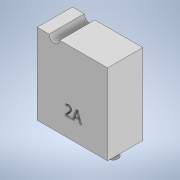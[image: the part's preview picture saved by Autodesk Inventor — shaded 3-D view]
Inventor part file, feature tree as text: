
AUTODESK INVENTOR PART (.ipt)
format: ipt  version: 2021 (Build 250183000, 183)  size: 163,328 bytes
history: native  units: mm
features: sketch x4, extrude x3, emboss x1
ambient origin geometry x8: Origin, YZ Plane, XZ Plane, XY Plane, X Axis, Y Axis, Z Axis, Center Point
bodies: Solid1 (feature_tree)
feature tree (8):
  extrude  "Extrusion1"  Depth=11.4385mm
  extrude  "Extrusion2"  Depth=5.0mm
  extrude  "Extrusion3"  Depth=3.0mm
  emboss  "Emboss1"
  sketch  "Sketch1"  dims[d0=22.877mm d1=11.4385mm]
  sketch  "Sketch2"  dims[d3=10.0mm d4=5.0mm]
  sketch  "Sketch3"  dims[d5=20.0mm d6=0.0mm d7=3.0mm]
  sketch  "Sketch4"  dims[d8=3.5mm d9=3.0mm d10=0.0mm d11=3.0mm d12=4.887mm d13=0.0mm d14=0.0mm d15=1.0mm d16=0.0mm]
